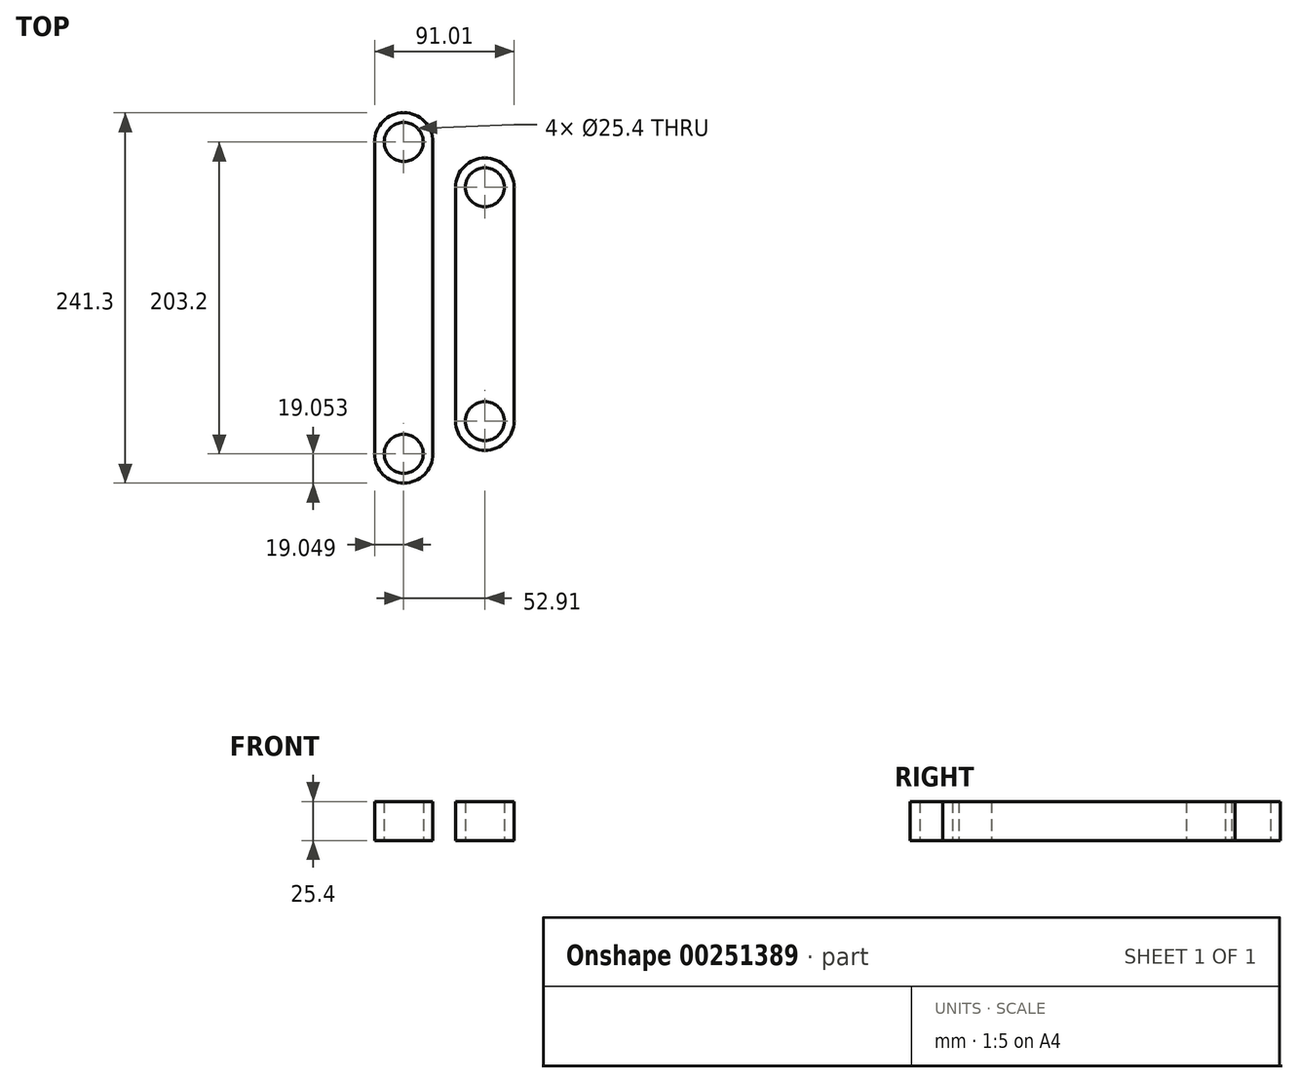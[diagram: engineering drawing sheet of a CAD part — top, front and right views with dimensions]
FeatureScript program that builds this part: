
annotation { "Feature Type Name" : "Feature", "Feature Type Description" : "" }
export const myFeature = defineFeature(function(context is Context, id is Id, definition is map)
    precondition{}
    {
        {
            var Q0;
            Q0=qCreatedBy(makeId("Top.planeOp"),FACE);
            var sketch = newSketch(context, id + "F0", { "sketchPlane" : qUnion([Q0])});
            skLineSegment(sketch, "E0.bottom", {"start": v(-27.08, 51.12) * mm, "end": v(-27.08, 51.12) * mm});
            skLineSegment(sketch, "E0.top", {"start": v(-27.08, -190.18) * mm, "end": v(-27.08, -190.18) * mm});
            skLineSegment(sketch, "E0.left", {"start": v(-46.13, 32.07) * mm, "end": v(-46.13, -171.13) * mm});
            skLineSegment(sketch, "E0.right", {"start": v(-8.03, 32.07) * mm, "end": v(-8.03, -171.13) * mm});
            skLineSegment(sketch, "E1.bottom", {"start": v(25.83, 21.65) * mm, "end": v(25.83, 21.65) * mm});
            skLineSegment(sketch, "E1.top", {"start": v(25.83, -168.85) * mm, "end": v(25.83, -168.85) * mm});
            skLineSegment(sketch, "E1.left", {"start": v(6.78, 2.6) * mm, "end": v(6.78, -149.8) * mm});
            skLineSegment(sketch, "E1.right", {"start": v(44.88, 2.6) * mm, "end": v(44.88, -149.8) * mm});
            skCircle(sketch, "E2", {"center": v(-27.08, 32.07) * mm, "radius": 12.7 * mm});
            skPoint(sketch, "E2.centerSnap0", {"position": v(-27.08, 51.12) * mm});
            skCircle(sketch, "E3", {"center": v(-27.08, -171.13) * mm, "radius": 12.7 * mm});
            skPoint(sketch, "E3.centerSnap0", {"position": v(-27.08, -190.18) * mm});
            skCircle(sketch, "E4", {"center": v(25.83, -149.8) * mm, "radius": 12.7 * mm});
            skPoint(sketch, "E4.centerSnap0", {"position": v(25.83, -168.85) * mm});
            skCircle(sketch, "E5", {"center": v(25.83, 2.6) * mm, "radius": 12.7 * mm});
            skPoint(sketch, "E5.centerSnap0", {"position": v(25.83, 21.65) * mm});
            skPoint(sketch, "E6.visualSharp", {"position": v(-46.13, 51.12) * mm});
            skArc(sketch, "E6.filletArc", {"start": v(-27.08, 51.12) * mm, "mid": v(-40.55, 45.54) * mm, "end": v(-46.13, 32.07) * mm});
            skPoint(sketch, "E7.visualSharp", {"position": v(-8.03, -190.18) * mm});
            skArc(sketch, "E7.filletArc", {"start": v(-27.08, -190.18) * mm, "mid": v(-13.61, -184.6) * mm, "end": v(-8.03, -171.13) * mm});
            skPoint(sketch, "E8.visualSharp", {"position": v(-46.13, -190.18) * mm});
            skArc(sketch, "E8.filletArc", {"start": v(-46.13, -171.13) * mm, "mid": v(-40.55, -184.6) * mm, "end": v(-27.08, -190.18) * mm});
            skPoint(sketch, "E9.visualSharp", {"position": v(-8.03, 51.12) * mm});
            skArc(sketch, "E9.filletArc", {"start": v(-8.03, 32.07) * mm, "mid": v(-13.61, 45.54) * mm, "end": v(-27.08, 51.12) * mm});
            skPoint(sketch, "E10.visualSharp", {"position": v(6.78, 21.65) * mm});
            skArc(sketch, "E10.filletArc", {"start": v(25.83, 21.65) * mm, "mid": v(12.36, 16.07) * mm, "end": v(6.78, 2.6) * mm});
            skPoint(sketch, "E11.visualSharp", {"position": v(44.88, 21.65) * mm});
            skArc(sketch, "E11.filletArc", {"start": v(44.88, 2.6) * mm, "mid": v(39.3, 16.07) * mm, "end": v(25.83, 21.65) * mm});
            skPoint(sketch, "E12.visualSharp", {"position": v(44.88, -168.85) * mm});
            skArc(sketch, "E12.filletArc", {"start": v(25.83, -168.85) * mm, "mid": v(39.3, -163.27) * mm, "end": v(44.88, -149.8) * mm});
            skPoint(sketch, "E13.visualSharp", {"position": v(6.78, -168.85) * mm});
            skArc(sketch, "E13.filletArc", {"start": v(6.78, -149.8) * mm, "mid": v(12.36, -163.27) * mm, "end": v(25.83, -168.85) * mm});
            skSolve(sketch);
        }
        {
            var Q0;
            Q0=makeQuery(id+"F0.imprint","IMPRINT",FACE,{"disambiguationData":[TD([[makeQuery(id+"F0.imprint","IMPRINT",EDGE,{"derivedFrom":sQuery(id+"F0.wireOp",EDGE,"E0.left")}),1.0]])]});
            extrude(context, id + "F1", {"entities" : qUnion([Q0]), "depth" : 25.4 * mm});
        }
        {
            var Q0;
            Q0=makeQuery(id+"F0.imprint","IMPRINT",FACE,{"disambiguationData":[TD([[makeQuery(id+"F0.imprint","IMPRINT",EDGE,{"derivedFrom":sQuery(id+"F0.wireOp",EDGE,"E1.left")}),1.0]])]});
            extrude(context, id + "F2", {"entities" : qUnion([Q0]), "depth" : 25.4 * mm});
        }
    });
